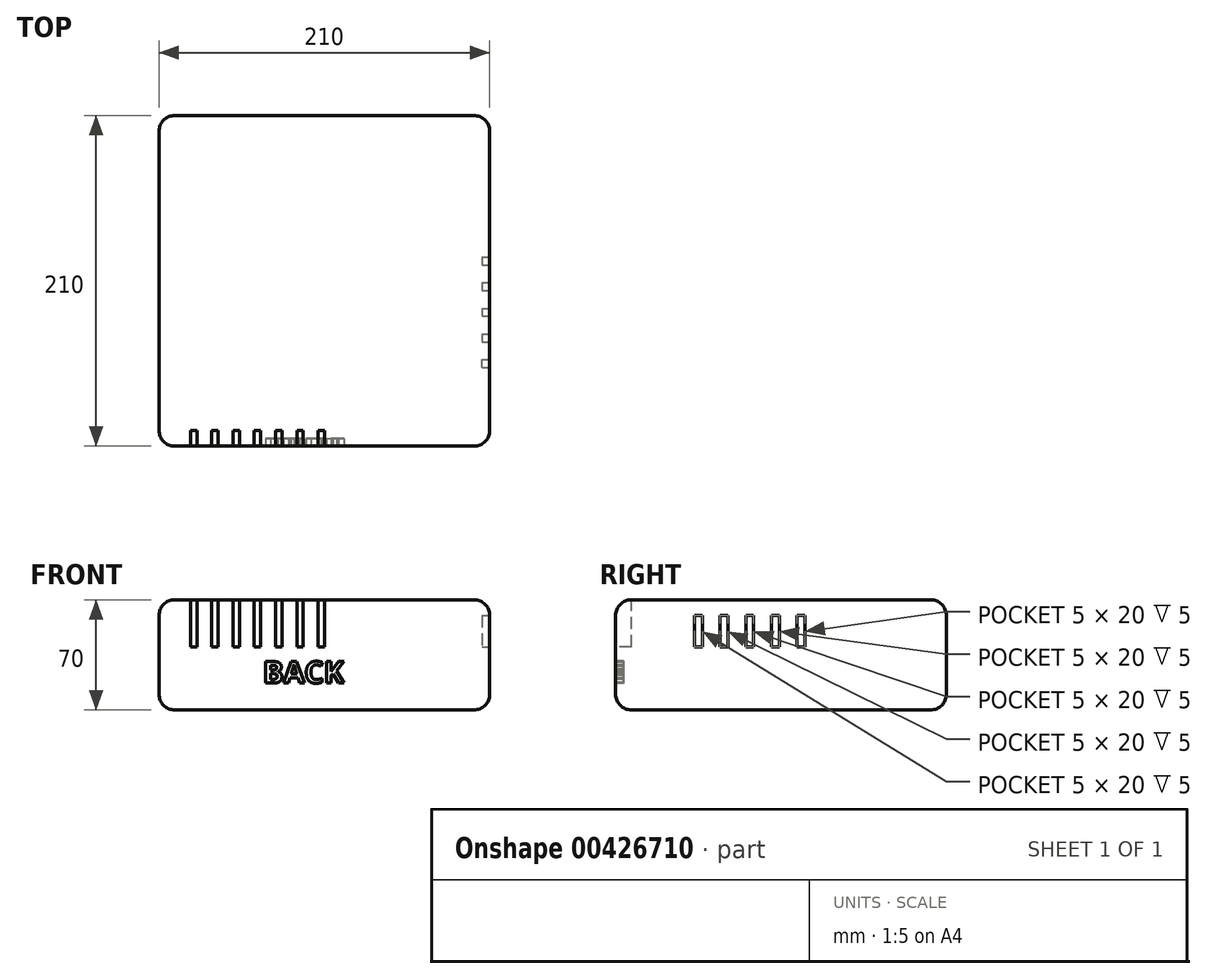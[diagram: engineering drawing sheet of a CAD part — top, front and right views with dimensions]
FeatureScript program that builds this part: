
annotation { "Feature Type Name" : "Feature", "Feature Type Description" : "" }
export const myFeature = defineFeature(function(context is Context, id is Id, definition is map)
    precondition{}
    {
        {
            var Q0;
            Q0=qCreatedBy(makeId("Top.planeOp"),FACE);
            var sketch = newSketch(context, id + "F0", { "sketchPlane" : qUnion([Q0])});
            skLineSegment(sketch, "E0.bottom", {"start": v(105, 105) * mm, "end": v(-105, 105) * mm});
            skLineSegment(sketch, "E0.top", {"start": v(105, -105) * mm, "end": v(-105, -105) * mm});
            skLineSegment(sketch, "E0.left", {"start": v(105, 105) * mm, "end": v(105, -105) * mm});
            skLineSegment(sketch, "E0.right", {"start": v(-105, 105) * mm, "end": v(-105, -105) * mm});
            skPoint(sketch, "E0.middle", {"position": v(0, 0) * mm});
            skSolve(sketch);
        }
        {
            var Q0;
            Q0=makeQuery(id+"F0.imprint","IMPRINT",FACE,{"disambiguationData":[TD([[makeQuery(id+"F0.imprint","IMPRINT",EDGE,{"derivedFrom":sQuery(id+"F0.wireOp",EDGE,"E0.bottom")}),1.0]])]});
            extrude(context, id + "F1", {"entities" : qUnion([Q0]), "depth" : 70 * mm});
        }
        {
            var Q0;
            Q0=makeQuery(id+"F1.opExtrude","SWEPT_EDGE",EDGE,{"disambiguationData":[OSD([sQuery(id+"F0.wireOp",EDGE,"E0.bottom"),sQuery(id+"F0.wireOp",EDGE,"E0.right")])]});
            var Q1;
            Q1=makeQuery(id+"F1.opExtrude","SWEPT_EDGE",EDGE,{"disambiguationData":[OSD([sQuery(id+"F0.wireOp",EDGE,"E0.bottom"),sQuery(id+"F0.wireOp",EDGE,"E0.left")])]});
            var Q2;
            Q2=makeQuery(id+"F1.opExtrude","SWEPT_EDGE",EDGE,{"disambiguationData":[OSD([sQuery(id+"F0.wireOp",EDGE,"E0.top"),sQuery(id+"F0.wireOp",EDGE,"E0.right")])]});
            var Q3;
            Q3=makeQuery(id+"F1.opExtrude","SWEPT_EDGE",EDGE,{"disambiguationData":[OSD([sQuery(id+"F0.wireOp",EDGE,"E0.top"),sQuery(id+"F0.wireOp",EDGE,"E0.left")])]});
            fillet(context, id + "F2", {"entities" : qUnion([Q0, Q1, Q2, Q3]), "radius" : 10 * mm, "tangentPropagation" : true, "allowEdgeOverflow" : false});
        }
        {
            var Q0;
            Q0=makeQuery(id+"F1.opExtrude","CAP_EDGE",EDGE,{"disambiguationData":[OSD([sQuery(id+"F0.wireOp",EDGE,"E0.left")])],"isStart":false});
            var Q1;
            Q1=makeQuery(id+"F1.opExtrude","CAP_EDGE",EDGE,{"disambiguationData":[OSD([sQuery(id+"F0.wireOp",EDGE,"E0.left")])],"isStart":true});
            fillet(context, id + "F3", {"entities" : qUnion([Q0, Q1]), "radius" : 10 * mm, "tangentPropagation" : true, "allowEdgeOverflow" : false});
        }
        {
            var Q0;
            Q0=makeQuery(id+"F1.opExtrude","SWEPT_FACE",FACE,{"disambiguationData":[OSD([sQuery(id+"F0.wireOp",EDGE,"E0.top")])]});
            var sketch = newSketch(context, id + "F4", { "sketchPlane" : qUnion([Q0])});
            skLineSegment(sketch, "E1.left", {"start": v(-85, 40) * mm, "end": v(-85, 70) * mm});
            skLineSegment(sketch, "E1.right", {"start": v(0, 40) * mm, "end": v(0, 70) * mm});
            skLineSegment(sketch, "E2.bottom", {"start": v(-85, 70) * mm, "end": v(-81, 70) * mm});
            skLineSegment(sketch, "E2.top", {"start": v(-85, 40) * mm, "end": v(-81, 40) * mm});
            skLineSegment(sketch, "E2.left", {"start": v(-85, 70) * mm, "end": v(-85, 40) * mm});
            skLineSegment(sketch, "E2.right", {"start": v(-81, 70) * mm, "end": v(-81, 40) * mm});
            skLineSegment(sketch, "E3.1.0.0", {"start": v(-71.5, 70) * mm, "end": v(-67.5, 70) * mm});
            skLineSegment(sketch, "E3.1.0.1", {"start": v(-71.5, 40) * mm, "end": v(-71.5, 70) * mm});
            skLineSegment(sketch, "E3.1.0.2", {"start": v(-67.5, 70) * mm, "end": v(-67.5, 40) * mm});
            skLineSegment(sketch, "E3.1.0.3", {"start": v(-71.5, 40) * mm, "end": v(-67.5, 40) * mm});
            skLineSegment(sketch, "E3.2.0.0", {"start": v(-58, 70) * mm, "end": v(-54, 70) * mm});
            skLineSegment(sketch, "E3.2.0.1", {"start": v(-58, 40) * mm, "end": v(-58, 70) * mm});
            skLineSegment(sketch, "E3.2.0.2", {"start": v(-54, 70) * mm, "end": v(-54, 40) * mm});
            skLineSegment(sketch, "E3.2.0.3", {"start": v(-58, 40) * mm, "end": v(-54, 40) * mm});
            skLineSegment(sketch, "E3.3.0.0", {"start": v(-44.5, 70) * mm, "end": v(-40.5, 70) * mm});
            skLineSegment(sketch, "E3.3.0.1", {"start": v(-44.5, 40) * mm, "end": v(-44.5, 70) * mm});
            skLineSegment(sketch, "E3.3.0.2", {"start": v(-40.5, 70) * mm, "end": v(-40.5, 40) * mm});
            skLineSegment(sketch, "E3.3.0.3", {"start": v(-44.5, 40) * mm, "end": v(-40.5, 40) * mm});
            skLineSegment(sketch, "E3.4.0.0", {"start": v(-31, 70) * mm, "end": v(-27, 70) * mm});
            skLineSegment(sketch, "E3.4.0.1", {"start": v(-31, 40) * mm, "end": v(-31, 70) * mm});
            skLineSegment(sketch, "E3.4.0.2", {"start": v(-27, 70) * mm, "end": v(-27, 40) * mm});
            skLineSegment(sketch, "E3.4.0.3", {"start": v(-31, 40) * mm, "end": v(-27, 40) * mm});
            skLineSegment(sketch, "E3.5.0.0", {"start": v(-17.5, 70) * mm, "end": v(-13.5, 70) * mm});
            skLineSegment(sketch, "E3.5.0.1", {"start": v(-17.5, 40) * mm, "end": v(-17.5, 70) * mm});
            skLineSegment(sketch, "E3.5.0.2", {"start": v(-13.5, 70) * mm, "end": v(-13.5, 40) * mm});
            skLineSegment(sketch, "E3.5.0.3", {"start": v(-17.5, 40) * mm, "end": v(-13.5, 40) * mm});
            skLineSegment(sketch, "E3.6.0.0", {"start": v(-4, 70) * mm, "end": v(0, 70) * mm});
            skLineSegment(sketch, "E3.6.0.1", {"start": v(-4, 40) * mm, "end": v(-4, 70) * mm});
            skLineSegment(sketch, "E3.6.0.2", {"start": v(0, 70) * mm, "end": v(0, 40) * mm});
            skLineSegment(sketch, "E3.6.0.3", {"start": v(-4, 40) * mm, "end": v(0, 40) * mm});
            skSolve(sketch);
        }
        {
            var Q0;
            Q0 = qSketchRegion(id + "F4", true);
            extrude(context, id + "F5", {"entities" : qUnion([Q0]), "operationType" : NewBodyOperationType.REMOVE, "oppositeDirection" : true, "depth" : 10 * mm});
        }
        {
            var Q0;
            Q0=makeQuery(id+"F1.opExtrude","SWEPT_FACE",FACE,{"disambiguationData":[OSD([sQuery(id+"F0.wireOp",EDGE,"E0.left")])]});
            var sketch = newSketch(context, id + "F6", { "sketchPlane" : qUnion([Q0])});
            skLineSegment(sketch, "E4", {"start": v(-105, 60) * mm, "end": v(-55, 60) * mm, "construction": true});
            skLineSegment(sketch, "E5", {"start": v(-55, 60) * mm, "end": v(-55, 70) * mm, "construction": true});
            skLineSegment(sketch, "E6.left", {"start": v(-55, 60) * mm, "end": v(-55, 40) * mm, "construction": true});
            skLineSegment(sketch, "E6.right", {"start": v(15, 60) * mm, "end": v(15, 40) * mm, "construction": true});
            skLineSegment(sketch, "E7.bottom", {"start": v(-55, 40) * mm, "end": v(-50, 40) * mm});
            skLineSegment(sketch, "E7.top", {"start": v(-55, 60) * mm, "end": v(-50, 60) * mm});
            skLineSegment(sketch, "E7.left", {"start": v(-55, 40) * mm, "end": v(-55, 60) * mm});
            skLineSegment(sketch, "E7.right", {"start": v(-50, 40) * mm, "end": v(-50, 60) * mm});
            skLineSegment(sketch, "E8.1.0.0", {"start": v(-38.7, 60) * mm, "end": v(-33.7, 60) * mm});
            skLineSegment(sketch, "E8.1.0.1", {"start": v(-38.7, 60) * mm, "end": v(-38.7, 40) * mm});
            skLineSegment(sketch, "E8.1.0.2", {"start": v(-33.7, 40) * mm, "end": v(-33.7, 60) * mm});
            skLineSegment(sketch, "E8.1.0.3", {"start": v(-38.7, 40) * mm, "end": v(-33.7, 40) * mm});
            skLineSegment(sketch, "E8.2.0.0", {"start": v(-22.4, 60) * mm, "end": v(-17.4, 60) * mm});
            skLineSegment(sketch, "E8.2.0.1", {"start": v(-22.4, 60) * mm, "end": v(-22.4, 40) * mm});
            skLineSegment(sketch, "E8.2.0.2", {"start": v(-17.4, 40) * mm, "end": v(-17.4, 60) * mm});
            skLineSegment(sketch, "E8.2.0.3", {"start": v(-22.4, 40) * mm, "end": v(-17.4, 40) * mm});
            skLineSegment(sketch, "E8.3.0.0", {"start": v(-6.1, 60) * mm, "end": v(-1.1, 60) * mm});
            skLineSegment(sketch, "E8.3.0.1", {"start": v(-6.1, 60) * mm, "end": v(-6.1, 40) * mm});
            skLineSegment(sketch, "E8.3.0.2", {"start": v(-1.1, 40) * mm, "end": v(-1.1, 60) * mm});
            skLineSegment(sketch, "E8.3.0.3", {"start": v(-6.1, 40) * mm, "end": v(-1.1, 40) * mm});
            skLineSegment(sketch, "E8.4.0.0", {"start": v(10.2, 60) * mm, "end": v(15.2, 60) * mm});
            skLineSegment(sketch, "E8.4.0.1", {"start": v(10.2, 60) * mm, "end": v(10.2, 40) * mm});
            skLineSegment(sketch, "E8.4.0.2", {"start": v(15.2, 40) * mm, "end": v(15.2, 60) * mm});
            skLineSegment(sketch, "E8.4.0.3", {"start": v(10.2, 40) * mm, "end": v(15.2, 40) * mm});
            skLineSegment(sketch, "E8.direction1", {"start": v(-55, 60) * mm, "end": v(-38.7, 60) * mm, "construction": true});
            skSolve(sketch);
        }
        {
            var Q0;
            Q0 = qSketchRegion(id + "F6", true);
            var Q1;
            Q1=sQuery(id+"F6.wireOp",EDGE,"E7.top");
            var Q2;
            Q2=sQuery(id+"F6.wireOp",EDGE,"E8.4.0.0");
            var Q3;
            Q3=sQuery(id+"F6.wireOp",EDGE,"E8.1.0.0");
            var Q4;
            Q4=sQuery(id+"F6.wireOp",EDGE,"E8.1.0.3");
            var Q5;
            Q5=sQuery(id+"F6.wireOp",EDGE,"E8.4.0.3");
            var Q6;
            Q6=sQuery(id+"F6.wireOp",EDGE,"E7.bottom");
            extrude(context, id + "F7", {"entities" : qUnion([Q0]), "operationType" : NewBodyOperationType.REMOVE, "surfaceEntities" : qUnion([Q1, Q2, Q3, Q4, Q5, Q6]), "oppositeDirection" : true, "depth" : 5 * mm});
        }
        {
            var Q0;
            Q0=makeQuery(id+"F1.opExtrude","SWEPT_FACE",FACE,{"disambiguationData":[OSD([sQuery(id+"F0.wireOp",EDGE,"E0.top")])]});
            var sketch = newSketch(context, id + "F8", { "sketchPlane" : qUnion([Q0])});
            skText(sketch, "E9", { "text": "BACK", "fontName": "OpenSans-Bold.ttf"});
            const initialGuessF8  = {"E9": [-0.03892, 0.01704, 1, 0, 0.01388]};
            skSetInitialGuess(sketch, initialGuessF8);
            skSolve(sketch);
        }
        {
            var Q0;
            Q0 = qSketchRegion(id + "F8", true);
            extrude(context, id + "F9", {"entities" : qUnion([Q0]), "operationType" : NewBodyOperationType.REMOVE, "oppositeDirection" : true, "depth" : 5 * mm});
        }
    });
